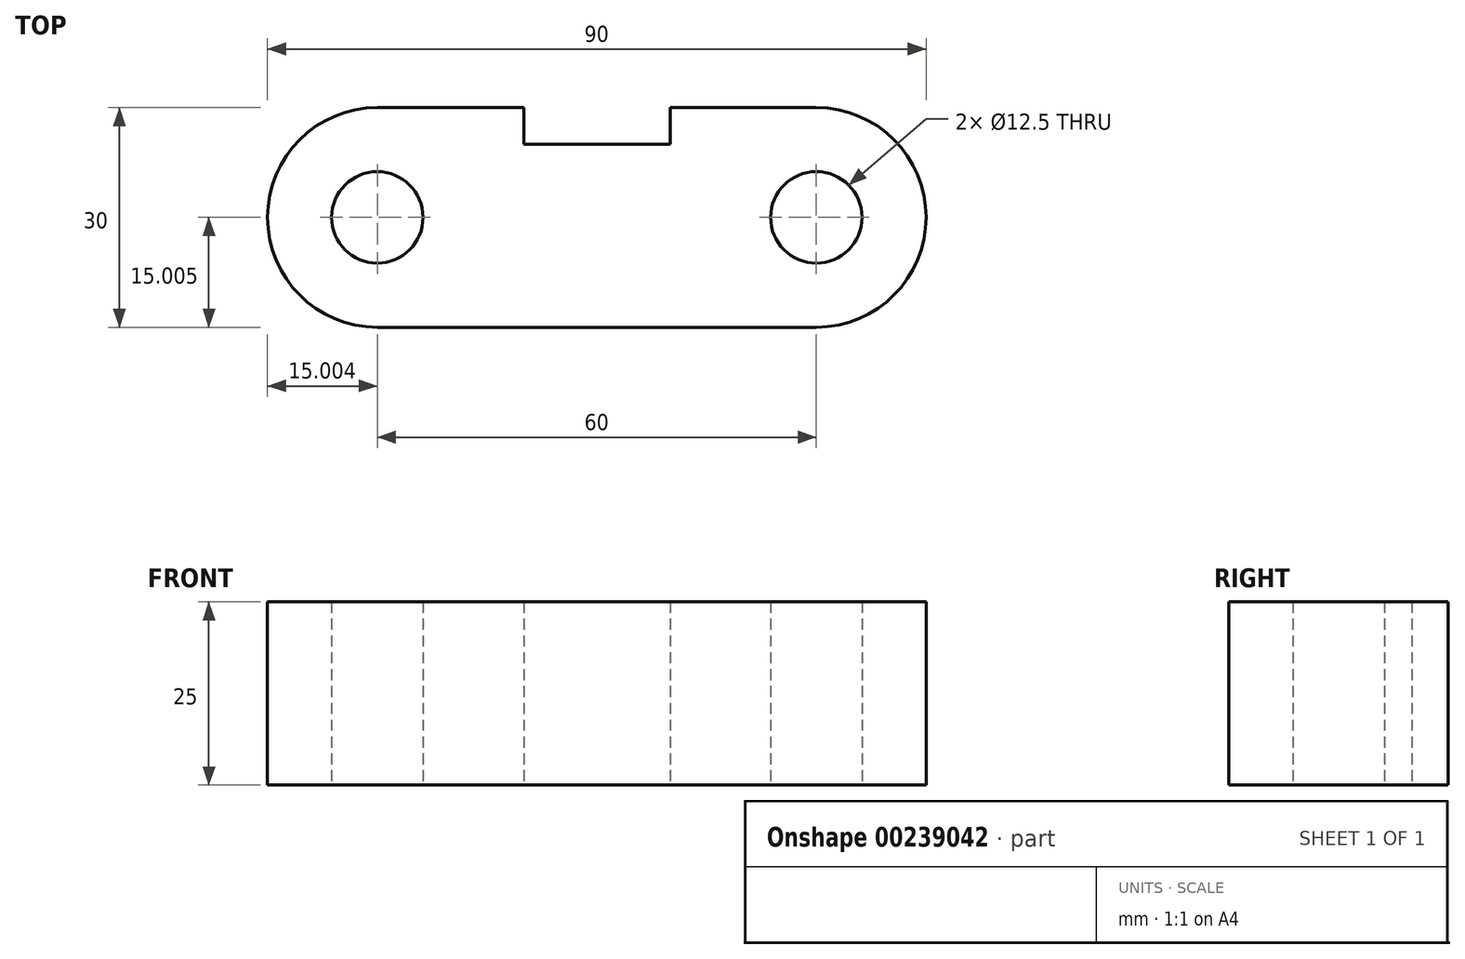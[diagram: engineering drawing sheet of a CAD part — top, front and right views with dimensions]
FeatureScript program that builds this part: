
annotation { "Feature Type Name" : "Feature", "Feature Type Description" : "" }
export const myFeature = defineFeature(function(context is Context, id is Id, definition is map)
    precondition{}
    {
        {
            var Q0;
            Q0=qCreatedBy(makeId("Top.planeOp"),FACE);
            var sketch = newSketch(context, id + "F0", { "sketchPlane" : qUnion([Q0])});
            skLineSegment(sketch, "E0", {"start": v(-35.13, -20.08) * mm, "end": v(24.87, -20.08) * mm});
            skLineSegment(sketch, "E1", {"start": v(39.87, -5.08) * mm, "end": v(39.87, -5.08) * mm});
            skLineSegment(sketch, "E2", {"start": v(-50.13, -5.08) * mm, "end": v(-50.13, -5.08) * mm});
            skPoint(sketch, "E3.visualSharp", {"position": v(-50.13, 9.92) * mm});
            skArc(sketch, "E3.filletArc", {"start": v(-35.13, 9.92) * mm, "mid": v(-45.73, 5.53) * mm, "end": v(-50.13, -5.08) * mm});
            skPoint(sketch, "E4.visualSharp", {"position": v(-50.13, -20.08) * mm});
            skArc(sketch, "E4.filletArc", {"start": v(-50.13, -5.08) * mm, "mid": v(-45.73, -15.68) * mm, "end": v(-35.13, -20.08) * mm});
            skPoint(sketch, "E5.visualSharp", {"position": v(39.87, -20.08) * mm});
            skArc(sketch, "E5.filletArc", {"start": v(24.87, -20.08) * mm, "mid": v(35.48, -15.68) * mm, "end": v(39.87, -5.08) * mm});
            skPoint(sketch, "E6.visualSharp", {"position": v(39.87, 9.92) * mm});
            skArc(sketch, "E6.filletArc", {"start": v(39.87, -5.08) * mm, "mid": v(35.48, 5.53) * mm, "end": v(24.87, 9.92) * mm});
            skCircle(sketch, "E7", {"center": v(-35.13, -5.08) * mm, "radius": 6.25 * mm});
            skCircle(sketch, "E8", {"center": v(24.87, -5.08) * mm, "radius": 6.25 * mm});
            skPoint(sketch, "E9.start.orphan", {"position": v(-10.13, 9.92) * mm});
            skLineSegment(sketch, "E10", {"start": v(-35.13, 9.92) * mm, "end": v(-15.13, 9.92) * mm});
            skLineSegment(sketch, "E11", {"start": v(-15.13, 9.92) * mm, "end": v(-15.13, 4.92) * mm});
            skLineSegment(sketch, "E12", {"start": v(-15.13, 4.92) * mm, "end": v(4.87, 4.92) * mm});
            skLineSegment(sketch, "E13", {"start": v(4.87, 4.92) * mm, "end": v(4.87, 9.92) * mm});
            skLineSegment(sketch, "E14", {"start": v(4.87, 9.92) * mm, "end": v(24.87, 9.92) * mm});
            skSolve(sketch);
        }
        {
            var Q0;
            Q0 = qSketchRegion(id + "F0", true);
            extrude(context, id + "F1", {"entities" : qUnion([Q0]), "depth" : 25 * mm});
        }
    });
